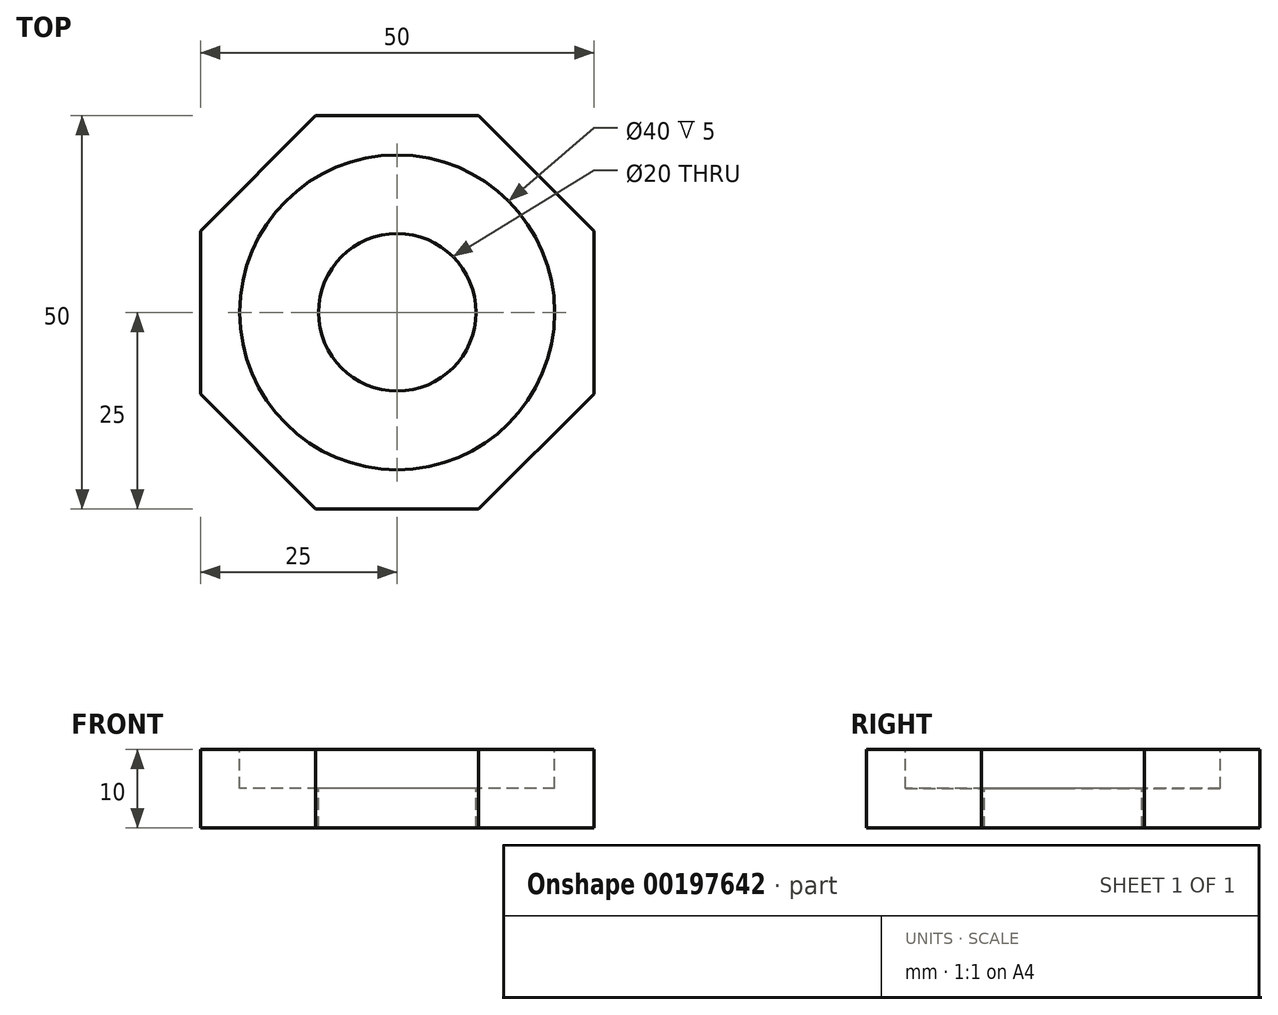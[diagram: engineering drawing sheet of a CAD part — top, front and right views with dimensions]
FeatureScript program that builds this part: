
annotation { "Feature Type Name" : "Feature", "Feature Type Description" : "" }
export const myFeature = defineFeature(function(context is Context, id is Id, definition is map)
    precondition{}
    {
        {
            var Q0;
            Q0=qCreatedBy(makeId("Top.planeOp"),FACE);
            var sketch = newSketch(context, id + "F0", { "sketchPlane" : qUnion([Q0])});
            skCircle(sketch, "E0.cCircle", {"center": v(0, 0) * mm, "radius": 25 * mm, "construction": true});
            skLineSegment(sketch, "E0.0", {"start": v(25, 10.36) * mm, "end": v(25, -10.36) * mm});
            skLineSegment(sketch, "E0.1", {"start": v(25, -10.36) * mm, "end": v(10.36, -25) * mm});
            skLineSegment(sketch, "E0.2", {"start": v(10.36, -25) * mm, "end": v(-10.36, -25) * mm});
            skLineSegment(sketch, "E0.3", {"start": v(-10.36, -25) * mm, "end": v(-25, -10.36) * mm});
            skLineSegment(sketch, "E0.4", {"start": v(-25, -10.36) * mm, "end": v(-25, 10.36) * mm});
            skLineSegment(sketch, "E0.5", {"start": v(-25, 10.36) * mm, "end": v(-10.36, 25) * mm});
            skLineSegment(sketch, "E0.6", {"start": v(-10.36, 25) * mm, "end": v(10.36, 25) * mm});
            skLineSegment(sketch, "E0.7", {"start": v(10.36, 25) * mm, "end": v(25, 10.36) * mm});
            skPoint(sketch, "E0.0.midPoint", {"position": v(25, 0) * mm});
            skSolve(sketch);
        }
        {
            var Q0;
            Q0=qSketchRegion(id+"F0",true);
            extrude(context, id + "F1", {"entities" : qUnion([Q0]), "depth" : 10 * mm});
        }
        {
            var Q0;
            Q0=makeQuery(id+"F1.opExtrude","CAP_FACE",FACE,{"disambiguationData":[OSD([sQuery(id+"F0.wireOp",EDGE,"E0.0"),sQuery(id+"F0.wireOp",EDGE,"E0.1"),sQuery(id+"F0.wireOp",EDGE,"E0.2"),sQuery(id+"F0.wireOp",EDGE,"E0.3"),sQuery(id+"F0.wireOp",EDGE,"E0.4"),sQuery(id+"F0.wireOp",EDGE,"E0.5"),sQuery(id+"F0.wireOp",EDGE,"E0.6"),sQuery(id+"F0.wireOp",EDGE,"E0.7")])],"isStart":false});
            var sketch = newSketch(context, id + "F2", { "sketchPlane" : qUnion([Q0])});
            skCircle(sketch, "E1", {"center": v(0, 0) * mm, "radius": 20 * mm});
            skSolve(sketch);
        }
        {
            var Q0;
            Q0=qSketchRegion(id+"F2",true);
            extrude(context, id + "F3", {"entities" : qUnion([Q0]), "operationType" : NewBodyOperationType.REMOVE, "oppositeDirection" : true, "depth" : 5 * mm});
        }
        {
            var Q0;
            Q0=makeQuery(id+"F1.opExtrude","CAP_FACE",FACE,{"disambiguationData":[OSD([sQuery(id+"F0.wireOp",EDGE,"E0.0"),sQuery(id+"F0.wireOp",EDGE,"E0.1"),sQuery(id+"F0.wireOp",EDGE,"E0.2"),sQuery(id+"F0.wireOp",EDGE,"E0.3"),sQuery(id+"F0.wireOp",EDGE,"E0.4"),sQuery(id+"F0.wireOp",EDGE,"E0.5"),sQuery(id+"F0.wireOp",EDGE,"E0.6"),sQuery(id+"F0.wireOp",EDGE,"E0.7")])],"isStart":false});
            var sketch = newSketch(context, id + "F4", { "sketchPlane" : qUnion([Q0])});
            skCircle(sketch, "E2", {"center": v(0, 0) * mm, "radius": 10 * mm});
            skSolve(sketch);
        }
        {
            var Q0;
            Q0=qSketchRegion(id+"F4",true);
            extrude(context, id + "F5", {"entities" : qUnion([Q0]), "operationType" : NewBodyOperationType.REMOVE, "oppositeDirection" : true, "depth" : 25 * mm});
        }
    });
